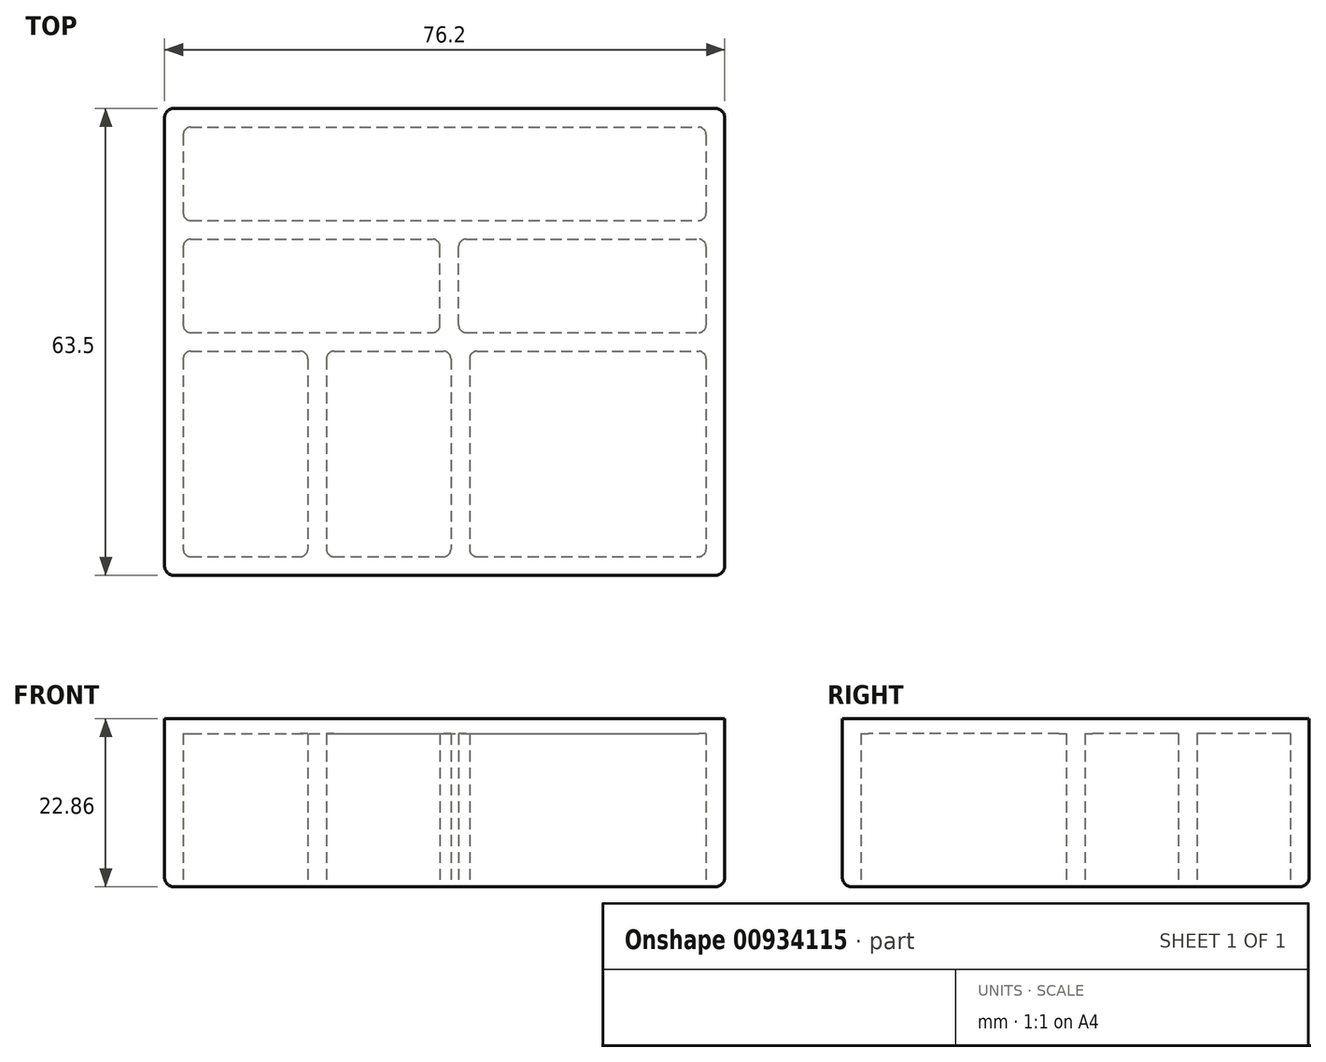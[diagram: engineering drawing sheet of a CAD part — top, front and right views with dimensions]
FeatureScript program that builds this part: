
annotation { "Feature Type Name" : "Feature", "Feature Type Description" : "" }
export const myFeature = defineFeature(function(context is Context, id is Id, definition is map)
    precondition{}
    {
        {
            var Q0;
            Q0=qCreatedBy(makeId("Top.planeOp"),FACE);
            var sketch = newSketch(context, id + "F0", { "sketchPlane" : qUnion([Q0])});
            skLineSegment(sketch, "E0.bottom", {"start": v(0, 0) * mm, "end": v(76.2, 0) * mm});
            skLineSegment(sketch, "E0.top", {"start": v(0, 63.5) * mm, "end": v(76.2, 63.5) * mm});
            skLineSegment(sketch, "E0.left", {"start": v(0, 0) * mm, "end": v(0, 63.5) * mm});
            skLineSegment(sketch, "E0.right", {"start": v(76.2, 0) * mm, "end": v(76.2, 63.5) * mm});
            skLineSegment(sketch, "E1.bottom", {"start": v(2.54, 60.96) * mm, "end": v(73.66, 60.96) * mm});
            skLineSegment(sketch, "E1.top", {"start": v(2.54, 2.54) * mm, "end": v(73.66, 2.54) * mm});
            skLineSegment(sketch, "E1.left", {"start": v(2.54, 60.96) * mm, "end": v(2.54, 2.54) * mm});
            skLineSegment(sketch, "E1.right", {"start": v(73.66, 60.96) * mm, "end": v(73.66, 2.54) * mm});
            skLineSegment(sketch, "E2.bottom", {"start": v(2.54, 48.26) * mm, "end": v(73.66, 48.26) * mm});
            skLineSegment(sketch, "E2.top", {"start": v(2.54, 45.72) * mm, "end": v(73.66, 45.72) * mm});
            skLineSegment(sketch, "E2.left", {"start": v(2.54, 48.26) * mm, "end": v(2.54, 45.72) * mm});
            skLineSegment(sketch, "E2.right", {"start": v(73.66, 48.26) * mm, "end": v(73.66, 45.72) * mm});
            skLineSegment(sketch, "E3.bottom", {"start": v(2.54, 33.02) * mm, "end": v(73.66, 33.02) * mm});
            skLineSegment(sketch, "E3.top", {"start": v(2.54, 30.48) * mm, "end": v(73.66, 30.48) * mm});
            skLineSegment(sketch, "E3.left", {"start": v(2.54, 33.02) * mm, "end": v(2.54, 30.48) * mm});
            skLineSegment(sketch, "E3.right", {"start": v(73.66, 33.02) * mm, "end": v(73.66, 30.48) * mm});
            skLineSegment(sketch, "E4.bottom", {"start": v(22.01, 30.48) * mm, "end": v(19.47, 30.48) * mm});
            skLineSegment(sketch, "E4.top", {"start": v(22.01, 2.54) * mm, "end": v(19.47, 2.54) * mm});
            skLineSegment(sketch, "E4.left", {"start": v(22.01, 30.48) * mm, "end": v(22.01, 2.54) * mm});
            skLineSegment(sketch, "E4.right", {"start": v(19.47, 30.48) * mm, "end": v(19.47, 2.54) * mm});
            skLineSegment(sketch, "E5.bottom", {"start": v(38.95, 30.48) * mm, "end": v(41.49, 30.48) * mm});
            skLineSegment(sketch, "E5.top", {"start": v(38.95, 2.54) * mm, "end": v(41.49, 2.54) * mm});
            skLineSegment(sketch, "E5.left", {"start": v(38.95, 30.48) * mm, "end": v(38.95, 2.54) * mm});
            skLineSegment(sketch, "E5.right", {"start": v(41.49, 30.48) * mm, "end": v(41.49, 2.54) * mm});
            skLineSegment(sketch, "E6.bottom", {"start": v(37.46, 33.02) * mm, "end": v(40, 33.02) * mm});
            skLineSegment(sketch, "E6.top", {"start": v(37.46, 45.72) * mm, "end": v(40, 45.72) * mm});
            skLineSegment(sketch, "E6.left", {"start": v(37.46, 33.02) * mm, "end": v(37.46, 45.72) * mm});
            skLineSegment(sketch, "E6.right", {"start": v(40, 33.02) * mm, "end": v(40, 45.72) * mm});
            skSolve(sketch);
        }
        {
            var Q0;
            Q0=makeQuery(id+"F0.imprint","IMPRINT",FACE,{"disambiguationData":[TD([[makeQuery(id+"F0.imprint","IMPRINT",EDGE,{"derivedFrom":sQuery(id+"F0.wireOp",EDGE,"E0.bottom")}),1.0]])]});
            var Q1;
            {var subQ4=sQuery(id+"F0.wireOp",EDGE,"E2.bottom");Q1=makeQuery(id+"F0.imprint","IMPRINT",FACE,{"disambiguationData":[TD([[makeQuery(id+"F0.imprint","IMPRINT",EDGE,{"derivedFrom":subQ4}),-1.0]])]});}
            var Q2;
            {var subQ4=sQuery(id+"F0.wireOp",EDGE,"E1.left");var subQ7=sQuery(id+"F0.wireOp",EDGE,"E3.top");var subQ8=makeQuery(id+"F0.imprint","INTERSECT",VERTEX,{"derivedFrom":[subQ4,subQ7]});Q2=makeQuery(id+"F0.imprint","IMPRINT",FACE,{"disambiguationData":[TD([[makeQuery(id+"F0.imprint","IMPRINT",EDGE,{"disambiguationData":[TD([[subQ8,1.0]])],"derivedFrom":subQ4}),1.0]])]});}
            var Q3;
            {var subQ0=sQuery(id+"F0.wireOp",EDGE,"E4.left");Q3=makeQuery(id+"F0.imprint","IMPRINT",FACE,{"disambiguationData":[TD([[makeQuery(id+"F0.imprint","IMPRINT",EDGE,{"derivedFrom":subQ0}),-1.0]])]});}
            var Q4;
            {var subQ2=sQuery(id+"F0.wireOp",EDGE,"E5.left");Q4=makeQuery(id+"F0.imprint","IMPRINT",FACE,{"disambiguationData":[TD([[makeQuery(id+"F0.imprint","IMPRINT",EDGE,{"derivedFrom":subQ2}),1.0]])]});}
            var Q5;
            {var subQ2=sQuery(id+"F0.wireOp",EDGE,"E6.left");Q5=makeQuery(id+"F0.imprint","IMPRINT",FACE,{"disambiguationData":[TD([[makeQuery(id+"F0.imprint","IMPRINT",EDGE,{"derivedFrom":subQ2}),-1.0]])]});}
            extrude(context, id + "F1", {"entities" : qUnion([Q0, Q1, Q2, Q3, Q4, Q5]), "depth" : 22.86 * mm, "offsetDistance" : 25.4 * mm});
        }
        {
            var Q0;
            Q0=makeQuery(id+"F1.opExtrude","CAP_FACE",FACE,{"disambiguationData":[OSD([sQuery(id+"F0.wireOp",EDGE,"E0.bottom"),sQuery(id+"F0.wireOp",EDGE,"E0.top"),sQuery(id+"F0.wireOp",EDGE,"E0.left"),sQuery(id+"F0.wireOp",EDGE,"E0.right"),sQuery(id+"F0.wireOp",EDGE,"E1.bottom"),sQuery(id+"F0.wireOp",EDGE,"E1.top"),sQuery(id+"F0.wireOp",EDGE,"E1.left"),sQuery(id+"F0.wireOp",EDGE,"E1.right"),sQuery(id+"F0.wireOp",EDGE,"E2.bottom"),sQuery(id+"F0.wireOp",EDGE,"E2.top"),sQuery(id+"F0.wireOp",EDGE,"E3.bottom"),sQuery(id+"F0.wireOp",EDGE,"E3.top"),sQuery(id+"F0.wireOp",EDGE,"E4.left"),sQuery(id+"F0.wireOp",EDGE,"E4.right"),sQuery(id+"F0.wireOp",EDGE,"E5.left"),sQuery(id+"F0.wireOp",EDGE,"E5.right"),sQuery(id+"F0.wireOp",EDGE,"E6.left"),sQuery(id+"F0.wireOp",EDGE,"E6.right")])],"isStart":false});
            var sketch = newSketch(context, id + "F2", { "sketchPlane" : qUnion([Q0])});
            skLineSegment(sketch, "E7.bottom", {"start": v(0, 63.5) * mm, "end": v(76.2, 63.5) * mm});
            skLineSegment(sketch, "E7.top", {"start": v(0, 0) * mm, "end": v(76.2, 0) * mm});
            skLineSegment(sketch, "E7.left", {"start": v(0, 63.5) * mm, "end": v(0, 0) * mm});
            skLineSegment(sketch, "E7.right", {"start": v(76.2, 63.5) * mm, "end": v(76.2, 0) * mm});
            skSolve(sketch);
        }
        {
            var Q0;
            Q0 = qSketchRegion(id + "F2", true);
            extrude(context, id + "F3", {"entities" : qUnion([Q0]), "operationType" : NewBodyOperationType.ADD, "oppositeDirection" : true, "depth" : 2.03 * mm, "offsetDistance" : 25.4 * mm});
        }
        {
            var Q0;
            Q0=makeQuery(id+"F1.opExtrude","CAP_EDGE",EDGE,{"disambiguationData":[OSD([sQuery(id+"F0.wireOp",EDGE,"E0.right")])],"isStart":true});
            var Q1;
            Q1=makeQuery(id+"F1.opExtrude","CAP_EDGE",EDGE,{"disambiguationData":[OSD([sQuery(id+"F0.wireOp",EDGE,"E0.bottom")])],"isStart":true});
            var Q2;
            Q2=makeQuery(id+"F1.opExtrude","CAP_EDGE",EDGE,{"disambiguationData":[OSD([sQuery(id+"F0.wireOp",EDGE,"E0.left")])],"isStart":true});
            var Q3;
            Q3=makeQuery(id+"F1.opExtrude","CAP_EDGE",EDGE,{"disambiguationData":[OSD([sQuery(id+"F0.wireOp",EDGE,"E0.top")])],"isStart":true});
            var Q4;
            Q4=makeQuery(id+"F1.opExtrude","SWEPT_EDGE",EDGE,{"disambiguationData":[OSD([sQuery(id+"F0.wireOp",EDGE,"E0.top"),sQuery(id+"F0.wireOp",EDGE,"E0.left")])]});
            var Q5;
            Q5=makeQuery(id+"F1.opExtrude","SWEPT_EDGE",EDGE,{"disambiguationData":[OSD([sQuery(id+"F0.wireOp",EDGE,"E0.top"),sQuery(id+"F0.wireOp",EDGE,"E0.right")])]});
            var Q6;
            Q6=makeQuery(id+"F1.opExtrude","SWEPT_EDGE",EDGE,{"disambiguationData":[OSD([sQuery(id+"F0.wireOp",EDGE,"E0.bottom"),sQuery(id+"F0.wireOp",EDGE,"E0.left")])]});
            var Q7;
            Q7=makeQuery(id+"F1.opExtrude","SWEPT_EDGE",EDGE,{"disambiguationData":[OSD([sQuery(id+"F0.wireOp",EDGE,"E0.bottom"),sQuery(id+"F0.wireOp",EDGE,"E0.right")])]});
            fillet(context, id + "F4", {"entities" : qUnion([Q0, Q1, Q2, Q3, Q4, Q5, Q6, Q7]), "radius" : 1.27 * mm, "tangentPropagation" : true, "allowEdgeOverflow" : false});
        }
        {
            var Q0;
            Q0=makeQuery(id+"F1.opExtrude","SWEPT_EDGE",EDGE,{"disambiguationData":[OSD([sQuery(id+"F0.wireOp",EDGE,"E1.bottom"),sQuery(id+"F0.wireOp",EDGE,"E1.right")])]});
            var Q1;
            Q1=makeQuery(id+"F1.opExtrude","SWEPT_EDGE",EDGE,{"disambiguationData":[OSD([sQuery(id+"F0.wireOp",EDGE,"E1.right"),sQuery(id+"F0.wireOp",EDGE,"E2.bottom")])]});
            var Q2;
            Q2=makeQuery(id+"F1.opExtrude","SWEPT_EDGE",EDGE,{"disambiguationData":[OSD([sQuery(id+"F0.wireOp",EDGE,"E1.right"),sQuery(id+"F0.wireOp",EDGE,"E3.bottom")])]});
            var Q3;
            Q3=makeQuery(id+"F1.opExtrude","SWEPT_EDGE",EDGE,{"disambiguationData":[OSD([sQuery(id+"F0.wireOp",EDGE,"E1.top"),sQuery(id+"F0.wireOp",EDGE,"E1.right")])]});
            var Q4;
            Q4=makeQuery(id+"F1.opExtrude","SWEPT_EDGE",EDGE,{"disambiguationData":[OSD([sQuery(id+"F0.wireOp",EDGE,"E1.top"),sQuery(id+"F0.wireOp",EDGE,"E5.left")])]});
            var Q5;
            Q5=makeQuery(id+"F1.opExtrude","SWEPT_EDGE",EDGE,{"disambiguationData":[OSD([sQuery(id+"F0.wireOp",EDGE,"E1.top"),sQuery(id+"F0.wireOp",EDGE,"E4.right")])]});
            var Q6;
            Q6=makeQuery(id+"F1.opExtrude","SWEPT_EDGE",EDGE,{"disambiguationData":[OSD([sQuery(id+"F0.wireOp",EDGE,"E3.top"),sQuery(id+"F0.wireOp",EDGE,"E4.right")])]});
            var Q7;
            Q7=makeQuery(id+"F1.opExtrude","SWEPT_EDGE",EDGE,{"disambiguationData":[OSD([sQuery(id+"F0.wireOp",EDGE,"E3.top"),sQuery(id+"F0.wireOp",EDGE,"E5.left")])]});
            var Q8;
            Q8=makeQuery(id+"F1.opExtrude","SWEPT_EDGE",EDGE,{"disambiguationData":[OSD([sQuery(id+"F0.wireOp",EDGE,"E1.left"),sQuery(id+"F0.wireOp",EDGE,"E3.top")])]});
            var Q9;
            Q9=makeQuery(id+"F1.opExtrude","SWEPT_EDGE",EDGE,{"disambiguationData":[OSD([sQuery(id+"F0.wireOp",EDGE,"E1.top"),sQuery(id+"F0.wireOp",EDGE,"E1.left")])]});
            var Q10;
            Q10=makeQuery(id+"F1.opExtrude","SWEPT_EDGE",EDGE,{"disambiguationData":[OSD([sQuery(id+"F0.wireOp",EDGE,"E1.left"),sQuery(id+"F0.wireOp",EDGE,"E2.top")])]});
            var Q11;
            Q11=makeQuery(id+"F1.opExtrude","SWEPT_EDGE",EDGE,{"disambiguationData":[OSD([sQuery(id+"F0.wireOp",EDGE,"E1.left"),sQuery(id+"F0.wireOp",EDGE,"E3.bottom")])]});
            var Q12;
            Q12=makeQuery(id+"F1.opExtrude","SWEPT_EDGE",EDGE,{"disambiguationData":[OSD([sQuery(id+"F0.wireOp",EDGE,"E1.right"),sQuery(id+"F0.wireOp",EDGE,"E2.top")])]});
            var Q13;
            Q13=makeQuery(id+"F1.opExtrude","SWEPT_EDGE",EDGE,{"disambiguationData":[OSD([sQuery(id+"F0.wireOp",EDGE,"E3.top"),sQuery(id+"F0.wireOp",EDGE,"E5.right")])]});
            var Q14;
            Q14=makeQuery(id+"F1.opExtrude","SWEPT_EDGE",EDGE,{"disambiguationData":[OSD([sQuery(id+"F0.wireOp",EDGE,"E1.top"),sQuery(id+"F0.wireOp",EDGE,"E5.right")])]});
            var Q15;
            Q15=makeQuery(id+"F1.opExtrude","SWEPT_EDGE",EDGE,{"disambiguationData":[OSD([sQuery(id+"F0.wireOp",EDGE,"E1.bottom"),sQuery(id+"F0.wireOp",EDGE,"E1.left")])]});
            var Q16;
            Q16=makeQuery(id+"F1.opExtrude","SWEPT_EDGE",EDGE,{"disambiguationData":[OSD([sQuery(id+"F0.wireOp",EDGE,"E1.left"),sQuery(id+"F0.wireOp",EDGE,"E2.bottom")])]});
            var Q17;
            Q17=makeQuery(id+"F1.opExtrude","SWEPT_EDGE",EDGE,{"disambiguationData":[OSD([sQuery(id+"F0.wireOp",EDGE,"E1.right"),sQuery(id+"F0.wireOp",EDGE,"E3.top")])]});
            var Q18;
            Q18=makeQuery(id+"F1.opExtrude","SWEPT_EDGE",EDGE,{"disambiguationData":[OSD([sQuery(id+"F0.wireOp",EDGE,"E1.top"),sQuery(id+"F0.wireOp",EDGE,"E4.left")])]});
            var Q19;
            Q19=makeQuery(id+"F1.opExtrude","SWEPT_EDGE",EDGE,{"disambiguationData":[OSD([sQuery(id+"F0.wireOp",EDGE,"E3.top"),sQuery(id+"F0.wireOp",EDGE,"E4.left")])]});
            var Q20;
            Q20=makeQuery(id+"F1.opExtrude","SWEPT_EDGE",EDGE,{"disambiguationData":[OSD([sQuery(id+"F0.wireOp",EDGE,"E3.bottom"),sQuery(id+"F0.wireOp",EDGE,"E6.right")])]});
            var Q21;
            Q21=makeQuery(id+"F1.opExtrude","SWEPT_EDGE",EDGE,{"disambiguationData":[OSD([sQuery(id+"F0.wireOp",EDGE,"E2.top"),sQuery(id+"F0.wireOp",EDGE,"E6.right")])]});
            var Q22;
            Q22=makeQuery(id+"F1.opExtrude","SWEPT_EDGE",EDGE,{"disambiguationData":[OSD([sQuery(id+"F0.wireOp",EDGE,"E2.top"),sQuery(id+"F0.wireOp",EDGE,"E6.left")])]});
            var Q23;
            Q23=makeQuery(id+"F1.opExtrude","SWEPT_EDGE",EDGE,{"disambiguationData":[OSD([sQuery(id+"F0.wireOp",EDGE,"E3.bottom"),sQuery(id+"F0.wireOp",EDGE,"E6.left")])]});
            fillet(context, id + "F5", {"entities" : qUnion([Q0, Q1, Q2, Q3, Q4, Q5, Q6, Q7, Q8, Q9, Q10, Q11, Q12, Q13, Q14, Q15, Q16, Q17, Q18, Q19, Q20, Q21, Q22, Q23]), "radius" : 1 * mm, "tangentPropagation" : true, "allowEdgeOverflow" : false});
        }
    });
